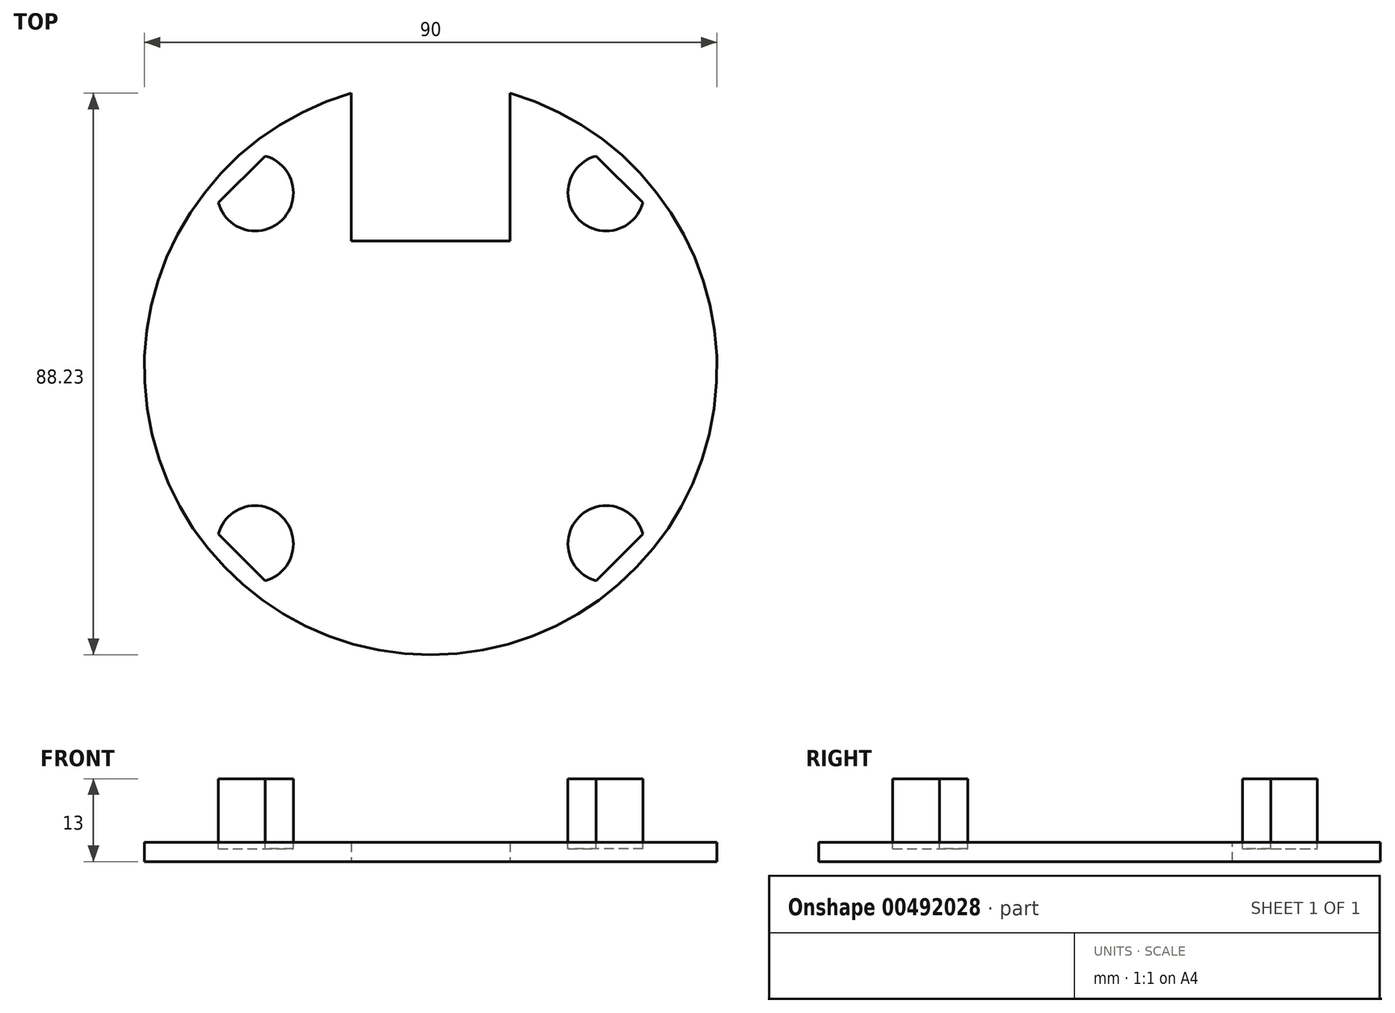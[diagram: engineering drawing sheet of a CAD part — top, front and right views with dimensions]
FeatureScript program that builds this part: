
annotation { "Feature Type Name" : "Feature", "Feature Type Description" : "" }
export const myFeature = defineFeature(function(context is Context, id is Id, definition is map)
    precondition{}
    {
        {
            var Q0;
            Q0=qCreatedBy(makeId("Top.planeOp"),FACE);
            var sketch = newSketch(context, id + "F0", { "sketchPlane" : qUnion([Q0])});
            skCircle(sketch, "E0", {"center": v(0, 0) * mm, "radius": 45 * mm});
            skSolve(sketch);
        }
        {
            var Q0;
            Q0 = qSketchRegion(id + "F0", true);
            extrude(context, id + "F1", {"entities" : qUnion([Q0]), "depth" : 3 * mm, "offsetDistance" : 25 * mm});
        }
        {
            var Q0;
            Q0=makeQuery(id+"F1.opExtrude","CAP_FACE",FACE,{"disambiguationData":[OSD([sQuery(id+"F0.wireOp",EDGE,"E0")])],"isStart":false});
            var sketch = newSketch(context, id + "F2", { "sketchPlane" : qUnion([Q0])});
            skLineSegment(sketch, "E1.bottom", {"start": v(-12.5, 70) * mm, "end": v(12.5, 70) * mm});
            skLineSegment(sketch, "E1.top", {"start": v(-12.5, 20) * mm, "end": v(12.5, 20) * mm});
            skLineSegment(sketch, "E1.left", {"start": v(-12.5, 70) * mm, "end": v(-12.5, 20) * mm});
            skLineSegment(sketch, "E1.right", {"start": v(12.5, 70) * mm, "end": v(12.5, 20) * mm});
            skPoint(sketch, "E1.middle", {"position": v(0, 45) * mm});
            skLineSegment(sketch, "E2", {"start": v(0, 0) * mm, "end": v(-59.88, 59.88) * mm, "construction": true});
            skArc(sketch, "E3", {"start": v(-33.37, 26.02) * mm, "mid": v(-23.33, 23.33) * mm, "end": v(-26.02, 33.37) * mm});
            skLineSegment(sketch, "E4", {"start": v(-33.37, 26.02) * mm, "end": v(-26.02, 33.37) * mm});
            skArc(sketch, "E5.1.0", {"start": v(-26.02, -33.37) * mm, "mid": v(-23.33, -23.33) * mm, "end": v(-33.37, -26.02) * mm});
            skLineSegment(sketch, "E5.1.1", {"start": v(-26.02, -33.37) * mm, "end": v(-33.37, -26.02) * mm});
            skArc(sketch, "E5.2.0", {"start": v(33.37, -26.02) * mm, "mid": v(23.33, -23.33) * mm, "end": v(26.02, -33.37) * mm});
            skLineSegment(sketch, "E5.2.1", {"start": v(33.37, -26.02) * mm, "end": v(26.02, -33.37) * mm});
            skArc(sketch, "E5.3.0", {"start": v(26.02, 33.37) * mm, "mid": v(23.33, 23.33) * mm, "end": v(33.37, 26.02) * mm});
            skLineSegment(sketch, "E5.3.1", {"start": v(26.02, 33.37) * mm, "end": v(33.37, 26.02) * mm});
            skPoint(sketch, "E5.center", {"position": v(0, 0) * mm});
            skSolve(sketch);
        }
        {
            var Q0;
            {var subQ0=sQuery(id+"F2.wireOp",EDGE,"E1.bottom");Q0=makeQuery(id+"F2.imprint","IMPRINT",FACE,{"disambiguationData":[TD([[makeQuery(id+"F2.imprint","IMPRINT",EDGE,{"derivedFrom":subQ0}),-1.0]])]});}
            var Q1;
            {var subQ0=sQuery(id+"F2.wireOp",EDGE,"E1.top");Q1=makeQuery(id+"F2.imprint","IMPRINT",FACE,{"disambiguationData":[TD([[makeQuery(id+"F2.imprint","IMPRINT",EDGE,{"derivedFrom":subQ0}),1.0]])]});}
            extrude(context, id + "F3", {"entities" : qUnion([Q0, Q1]), "operationType" : NewBodyOperationType.REMOVE, "oppositeDirection" : true, "depth" : 25 * mm, "offsetDistance" : 25 * mm});
        }
        {
            var Q0;
            Q0=makeQuery(id+"F2.imprint","IMPRINT",FACE,{"disambiguationData":[TD([[makeQuery(id+"F2.imprint","IMPRINT",EDGE,{"derivedFrom":sQuery(id+"F2.wireOp",EDGE,"E3")}),1.0]])]});
            var Q1;
            Q1=makeQuery(id+"F2.imprint","IMPRINT",FACE,{"disambiguationData":[TD([[makeQuery(id+"F2.imprint","IMPRINT",EDGE,{"derivedFrom":sQuery(id+"F2.wireOp",EDGE,"E5.3.0")}),1.0]])]});
            var Q2;
            Q2=makeQuery(id+"F2.imprint","IMPRINT",FACE,{"disambiguationData":[TD([[makeQuery(id+"F2.imprint","IMPRINT",EDGE,{"derivedFrom":sQuery(id+"F2.wireOp",EDGE,"E5.1.0")}),1.0]])]});
            var Q3;
            Q3=makeQuery(id+"F2.imprint","IMPRINT",FACE,{"disambiguationData":[TD([[makeQuery(id+"F2.imprint","IMPRINT",EDGE,{"derivedFrom":sQuery(id+"F2.wireOp",EDGE,"E5.2.0")}),1.0]])]});
            extrude(context, id + "F4", {"entities" : qUnion([Q0, Q1, Q2, Q3]), "depth" : 10 * mm, "offsetDistance" : 25 * mm});
        }
        {
            var Q0;
            Q0=makeQuery(id+"F2.imprint","IMPRINT",FACE,{"disambiguationData":[TD([[makeQuery(id+"F2.imprint","IMPRINT",EDGE,{"derivedFrom":sQuery(id+"F2.wireOp",EDGE,"E3")}),1.0]])]});
            var Q1;
            Q1=makeQuery(id+"F2.imprint","IMPRINT",FACE,{"disambiguationData":[TD([[makeQuery(id+"F2.imprint","IMPRINT",EDGE,{"derivedFrom":sQuery(id+"F2.wireOp",EDGE,"E5.1.0")}),1.0]])]});
            var Q2;
            Q2=makeQuery(id+"F2.imprint","IMPRINT",FACE,{"disambiguationData":[TD([[makeQuery(id+"F2.imprint","IMPRINT",EDGE,{"derivedFrom":sQuery(id+"F2.wireOp",EDGE,"E5.2.0")}),1.0]])]});
            var Q3;
            Q3=makeQuery(id+"F2.imprint","IMPRINT",FACE,{"disambiguationData":[TD([[makeQuery(id+"F2.imprint","IMPRINT",EDGE,{"derivedFrom":sQuery(id+"F2.wireOp",EDGE,"E5.3.0")}),1.0]])]});
            extrude(context, id + "F5", {"entities" : qUnion([Q0, Q1, Q2, Q3]), "operationType" : NewBodyOperationType.REMOVE, "oppositeDirection" : true, "depth" : 1 * mm, "offsetDistance" : 25 * mm});
        }
    });
